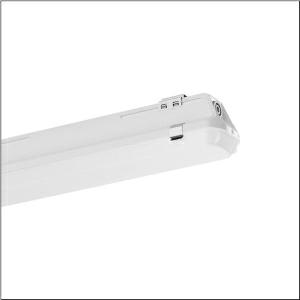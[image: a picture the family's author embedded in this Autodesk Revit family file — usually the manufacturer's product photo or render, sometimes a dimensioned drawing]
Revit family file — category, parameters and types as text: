
# Revit family: monsun_21_51fb107p660c
name_source: partatom
category: Lighting Fixtures
units: mm (PartAtom-declared; Revit-internal decimal feet)

## family parameters
Cut with Voids When Loaded = No
Host = Face
Light Source = No
Part Type = Normal
Room Calculation Point = No
Round Connector Dimension = Use Diameter
Shared = No

## types (1)
- Monsun 21 (1 x LED, 6010 lm, 34.9 W, 6500K)
    Apparent Load = 35 VA
    CIE Flux Codes = 47 77 93 94 100
    Color Rendering = 80
    Color Temperature = 6500K
    Default Elevation = 1800 mm
    Description = Monsun 21, damp-proof luminaire, chain hanger, primary optical cover: enclosure, of PMMA, light emission: direct distribution, primary light characteristic: symmetric, installation type: suspended mounting, surface-mounted, horizontal mounting, vertical mounting, LED, rated luminous flux: 6.010lm, luminous efficacy: 172lm/W, light colour: 865, colour temperature: 6500K, control gear: ON/OFF, with terminal, 3-pole, max. 2.5mm², mains connection: 220..240V, AC, 50/60Hz, rated input power: 35W, housing, of glass-fibre reinforced polyester, uncoated, bright grey, incl. chain hanger, length: 1.590mm, width: 90mm, height: 88mm, clip for enclosure, of stainless steel (V2A), ceiling mounting element, of stainless steel (V2A), chain hanger, of stainless steel (V2A), protection rating (complete): IP66, insulation class (complete): insulation class I (protective earthing), certification: CE, ENEC, VDE, UKCA, protection symbol: D, impact resistance: IK04, permissible operating ambient temperature: -25..+35°C, standard: EN 50419, EN 60598-2-1, corresponds to IFS (International Featured Standards) requirements for safety and quality in the food industry, for indoor or canopied outdoor use, no direct snow, no direct sun, no direct rain, LABS conformity tested according to VDMA 24364:2018-05, contact your sales advisor before using the luminaires in applications with unclear chemical exposure, large temperature fluctuations or condensation-forming humidity, packaging unit: 1 piece
    Height = 89 mm
    Lamp = 1 x LED
    Lamp Light Flux = 6010 lm
    Lamp Power = 34.9 W
    Lamp count = 1
    Length = 1590 mm
    Luminous efficacy = 172 lm/W
    Manufacturer = Siteco
    ModVariant = No
    Model = 51FB107P660C
    Mounting Place = Ceiling
    Mounting Type = Surface mounted
    Number of Poles = 1
    OnlyDefault = Yes
    Power Factor = 1
    Product Name = Monsun 21
    Product group = damp-proof luminaire
    ProductGroupID = 300
    Protection Class = Protection class I
    Protection Degree = IP 66
    RLX_Detail_Level = 1
    RLX_Emergency_Light_Flux = 0 lm
    RLX_Emergency_Type = 0
    RLX_Emergency_Type_DB = No
    RlxData = <blob elided: 88325 chars, md5=9f94d9ce>
    Socket = socket
    Standby Power = 0 W
    System Light Flux = 6010 lm
    System Power = 35 W
    Type Comments = Product without accessories
    Type Image = l_1319656.jpg
    URL = http://relux.com
    VarID = ---
    Voltage = 0 V
    Weight = 0.00 kg
    Width = 90 mm

## geometry (parser evidence)
native form markers: Blend x4, Sweep x14
no freeform markers — native parametric forms only
